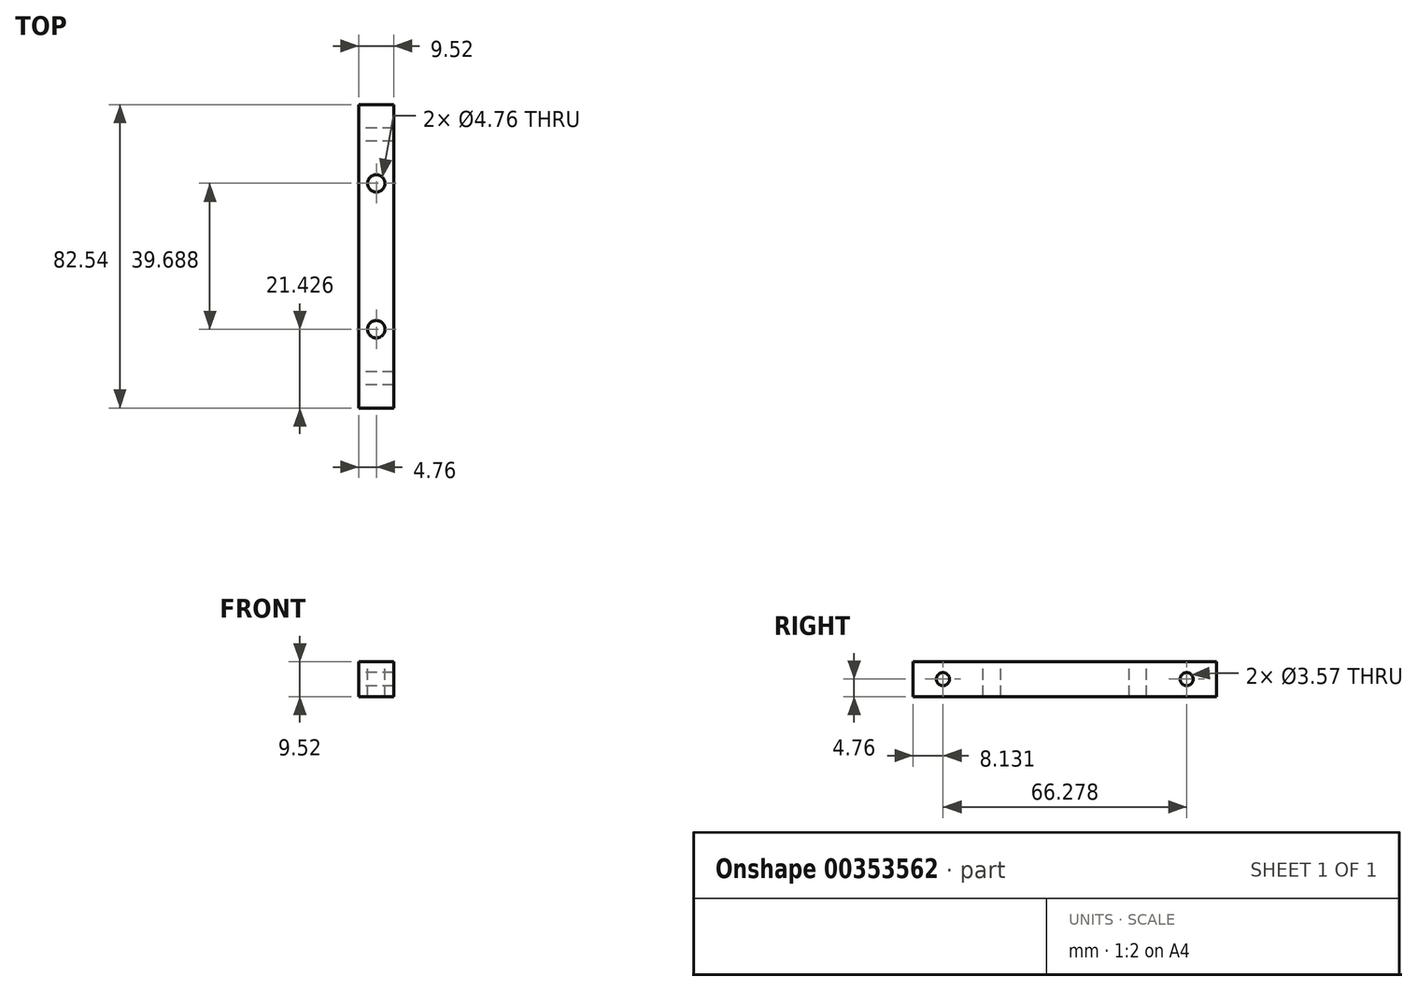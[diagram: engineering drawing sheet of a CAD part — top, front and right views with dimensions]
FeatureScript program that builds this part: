
annotation { "Feature Type Name" : "Feature", "Feature Type Description" : "" }
export const myFeature = defineFeature(function(context is Context, id is Id, definition is map)
    precondition{}
    {
        {
            var Q0;
            Q0=qCreatedBy(makeId("Front.planeOp"),FACE);
            var sketch = newSketch(context, id + "F0", { "sketchPlane" : qUnion([Q0])});
            skLineSegment(sketch, "E0.bottom", {"start": v(4.76, 4.76) * mm, "end": v(-4.76, 4.76) * mm});
            skLineSegment(sketch, "E0.top", {"start": v(4.76, -4.76) * mm, "end": v(-4.76, -4.76) * mm});
            skLineSegment(sketch, "E0.left", {"start": v(4.76, 4.76) * mm, "end": v(4.76, -4.76) * mm});
            skLineSegment(sketch, "E0.right", {"start": v(-4.76, 4.76) * mm, "end": v(-4.76, -4.76) * mm});
            skPoint(sketch, "E0.middle", {"position": v(0, 0) * mm});
            skSolve(sketch);
        }
        {
            var Q0;
            Q0 = qSketchRegion(id + "F0", true);
            extrude(context, id + "F1", {"entities" : qUnion([Q0]), "depth" : 82.55 * mm, "symmetric" : true});
        }
        {
            var Q0;
            Q0=makeQuery(id+"F1.opExtrude","SWEPT_FACE",FACE,{"disambiguationData":[OSD([sQuery(id+"F0.wireOp",EDGE,"E0.right")])]});
            var sketch = newSketch(context, id + "F2", { "sketchPlane" : qUnion([Q0])});
            skCircle(sketch, "E1", {"center": v(-33.14, 0) * mm, "radius": 1.79 * mm});
            skCircle(sketch, "E2", {"center": v(33.14, 0) * mm, "radius": 1.79 * mm});
            skSolve(sketch);
        }
        {
            var Q0;
            Q0 = qSketchRegion(id + "F2", true);
            extrude(context, id + "F3", {"entities" : qUnion([Q0]), "operationType" : NewBodyOperationType.REMOVE, "endBound" : BoundingType.THROUGH_ALL, "oppositeDirection" : true, "depth" : 25.4 * mm});
        }
        {
            var Q0;
            Q0=makeQuery(id+"F1.opExtrude","SWEPT_FACE",FACE,{"disambiguationData":[OSD([sQuery(id+"F0.wireOp",EDGE,"E0.bottom")])]});
            var sketch = newSketch(context, id + "F4", { "sketchPlane" : qUnion([Q0])});
            skCircle(sketch, "E3", {"center": v(0, 19.84) * mm, "radius": 2.38 * mm});
            skCircle(sketch, "E4", {"center": v(0, -19.84) * mm, "radius": 2.38 * mm});
            skSolve(sketch);
        }
        {
            var Q0;
            Q0 = qSketchRegion(id + "F4", true);
            extrude(context, id + "F5", {"entities" : qUnion([Q0]), "operationType" : NewBodyOperationType.REMOVE, "endBound" : BoundingType.THROUGH_ALL, "oppositeDirection" : true, "depth" : 25.4 * mm});
        }
    });
